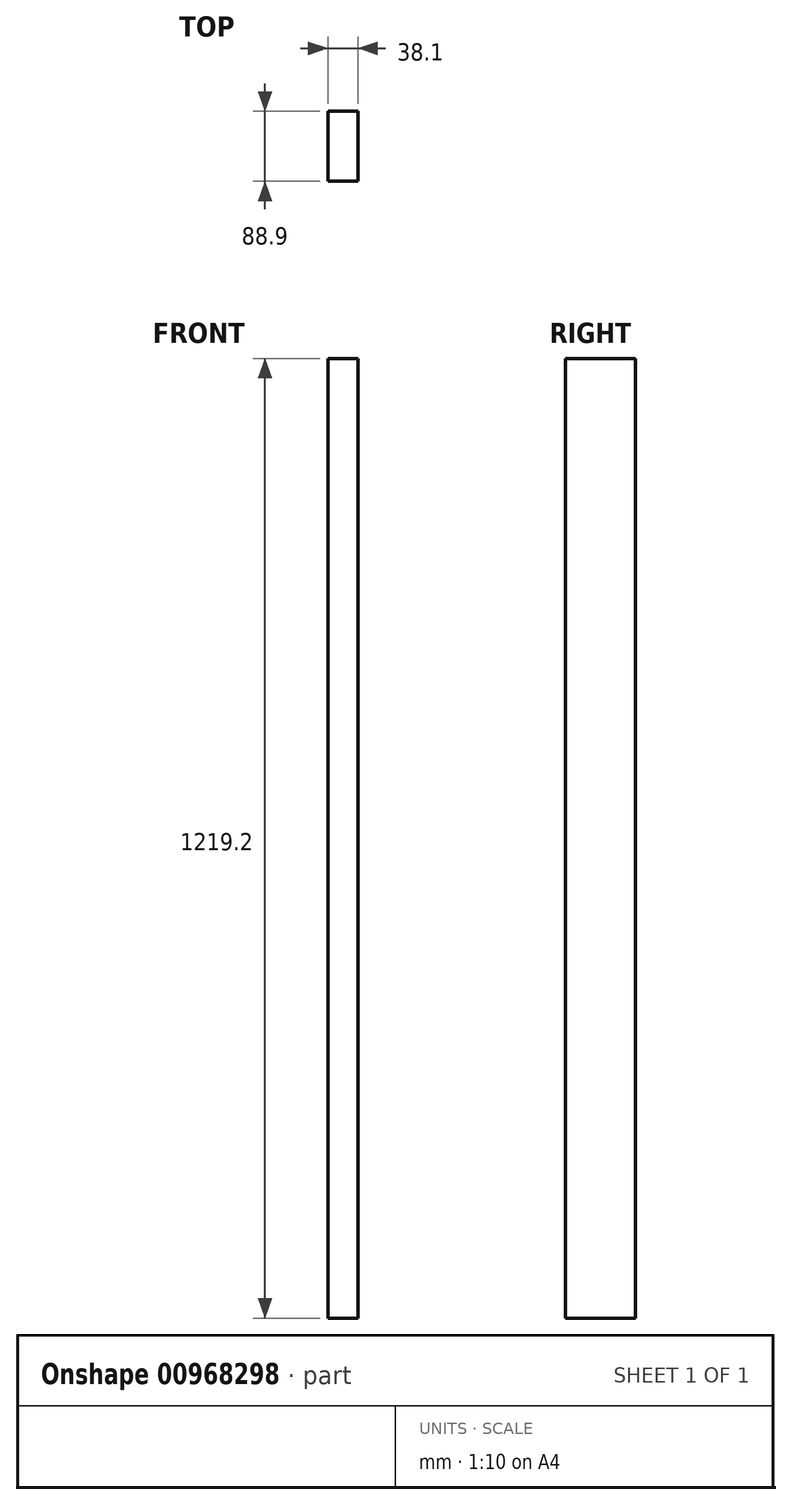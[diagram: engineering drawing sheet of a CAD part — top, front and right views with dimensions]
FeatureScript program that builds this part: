
annotation { "Feature Type Name" : "Feature", "Feature Type Description" : "" }
export const myFeature = defineFeature(function(context is Context, id is Id, definition is map)
    precondition{}
    {
        {
            var Q0;
            Q0=qCreatedBy(makeId("Top.planeOp"),FACE);
            var sketch = newSketch(context, id + "F0", { "sketchPlane" : qUnion([Q0])});
            skLineSegment(sketch, "E0.bottom", {"start": v(19.05, 44.45) * mm, "end": v(-19.05, 44.45) * mm});
            skLineSegment(sketch, "E0.top", {"start": v(19.05, -44.45) * mm, "end": v(-19.05, -44.45) * mm});
            skLineSegment(sketch, "E0.left", {"start": v(19.05, 44.45) * mm, "end": v(19.05, -44.45) * mm});
            skLineSegment(sketch, "E0.right", {"start": v(-19.05, 44.45) * mm, "end": v(-19.05, -44.45) * mm});
            skPoint(sketch, "E0.middle", {"position": v(0, 0) * mm});
            skSolve(sketch);
        }
        {
            var Q0;
            Q0=makeQuery(id+"F0.imprint","IMPRINT",FACE,{"disambiguationData":[TD([[makeQuery(id+"F0.imprint","IMPRINT",EDGE,{"derivedFrom":sQuery(id+"F0.wireOp",EDGE,"E0.bottom")}),1.0]])]});
            extrude(context, id + "F1", {"entities" : qUnion([Q0]), "endBound" : BoundingType.SYMMETRIC, "depth" : 1219.2 * mm, "offsetDistance" : 25.4 * mm});
        }
    });
